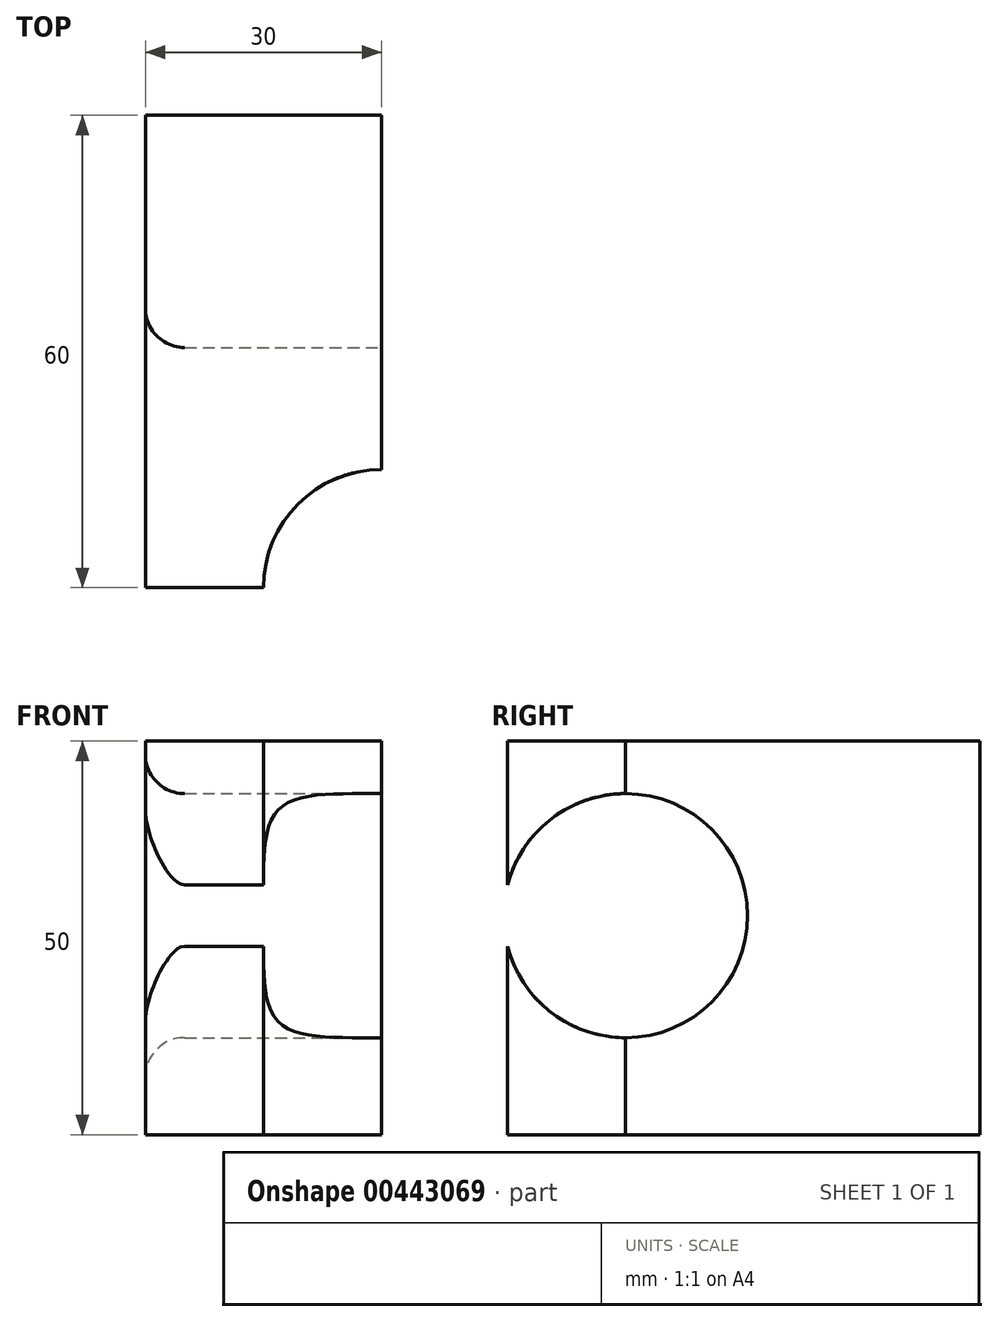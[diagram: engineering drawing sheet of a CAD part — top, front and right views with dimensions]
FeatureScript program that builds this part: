
annotation { "Feature Type Name" : "Feature", "Feature Type Description" : "" }
export const myFeature = defineFeature(function(context is Context, id is Id, definition is map)
    precondition{}
    {
        {
            var Q0;
            Q0=qCreatedBy(makeId("Top.planeOp"),FACE);
            var sketch = newSketch(context, id + "F0", { "sketchPlane" : qUnion([Q0])});
            skLineSegment(sketch, "E0.bottom", {"start": v(-25.25, -28.93) * mm, "end": v(4.75, -28.93) * mm});
            skLineSegment(sketch, "E0.top", {"start": v(-25.25, 31.07) * mm, "end": v(4.75, 31.07) * mm});
            skLineSegment(sketch, "E0.left", {"start": v(-25.25, -28.93) * mm, "end": v(-25.25, 31.07) * mm});
            skLineSegment(sketch, "E0.right", {"start": v(4.75, -28.93) * mm, "end": v(4.75, 31.07) * mm});
            skCircle(sketch, "E1", {"center": v(4.75, -28.93) * mm, "radius": 15 * mm});
            skSolve(sketch);
        }
        {
            var Q0;
            {var subQ1=sQuery(id+"F0.wireOp",EDGE,"E0.top");Q0=makeQuery(id+"F0.imprint","IMPRINT",FACE,{"disambiguationData":[TD([[makeQuery(id+"F0.imprint","IMPRINT",EDGE,{"derivedFrom":subQ1}),-1.0]])]});}
            extrude(context, id + "F1", {"entities" : qUnion([Q0]), "depth" : 50 * mm});
        }
        {
            var Q0;
            Q0=makeQuery(id+"F1.opExtrude","SWEPT_FACE",FACE,{"disambiguationData":[OSD([sQuery(id+"F0.wireOp",EDGE,"E0.right")])]});
            var sketch = newSketch(context, id + "F2", { "sketchPlane" : qUnion([Q0])});
            skCircle(sketch, "E2", {"center": v(-13.93, 27.82) * mm, "radius": 15.5 * mm});
            skSolve(sketch);
        }
        {
            var Q0;
            Q0 = qSketchRegion(id + "F2", true);
            extrude(context, id + "F3", {"entities" : qUnion([Q0]), "operationType" : NewBodyOperationType.REMOVE, "oppositeDirection" : true, "depth" : 70 * mm});
        }
        {
            var Q0;
            Q0=makeQuery(id+"F3.boolean.opBoolean","COPY",EDGE,{"derivedFrom":makeQuery(id+"F3.opExtrude","CAP_EDGE",EDGE,{"disambiguationData":[OSD([sQuery(id+"F2.wireOp",EDGE,"E2")])],"isStart":true})});
            var Q1;
            Q1=makeQuery(id+"F3.boolean.opBoolean","INTERSECT",EDGE,{"derivedFrom":[makeQuery(id+"F1.opExtrude","SWEPT_FACE",FACE,{"disambiguationData":[OSD([sQuery(id+"F0.wireOp",EDGE,"E0.left")])]}),makeQuery(id+"F3.opExtrude","SWEPT_FACE",FACE,{"disambiguationData":[OSD([sQuery(id+"F2.wireOp",EDGE,"E2")])]})]});
            fillet(context, id + "F4", {"entities" : qUnion([Q0, Q1]), "radius" : 5 * mm, "tangentPropagation" : true, "allowEdgeOverflow" : false});
        }
    });
